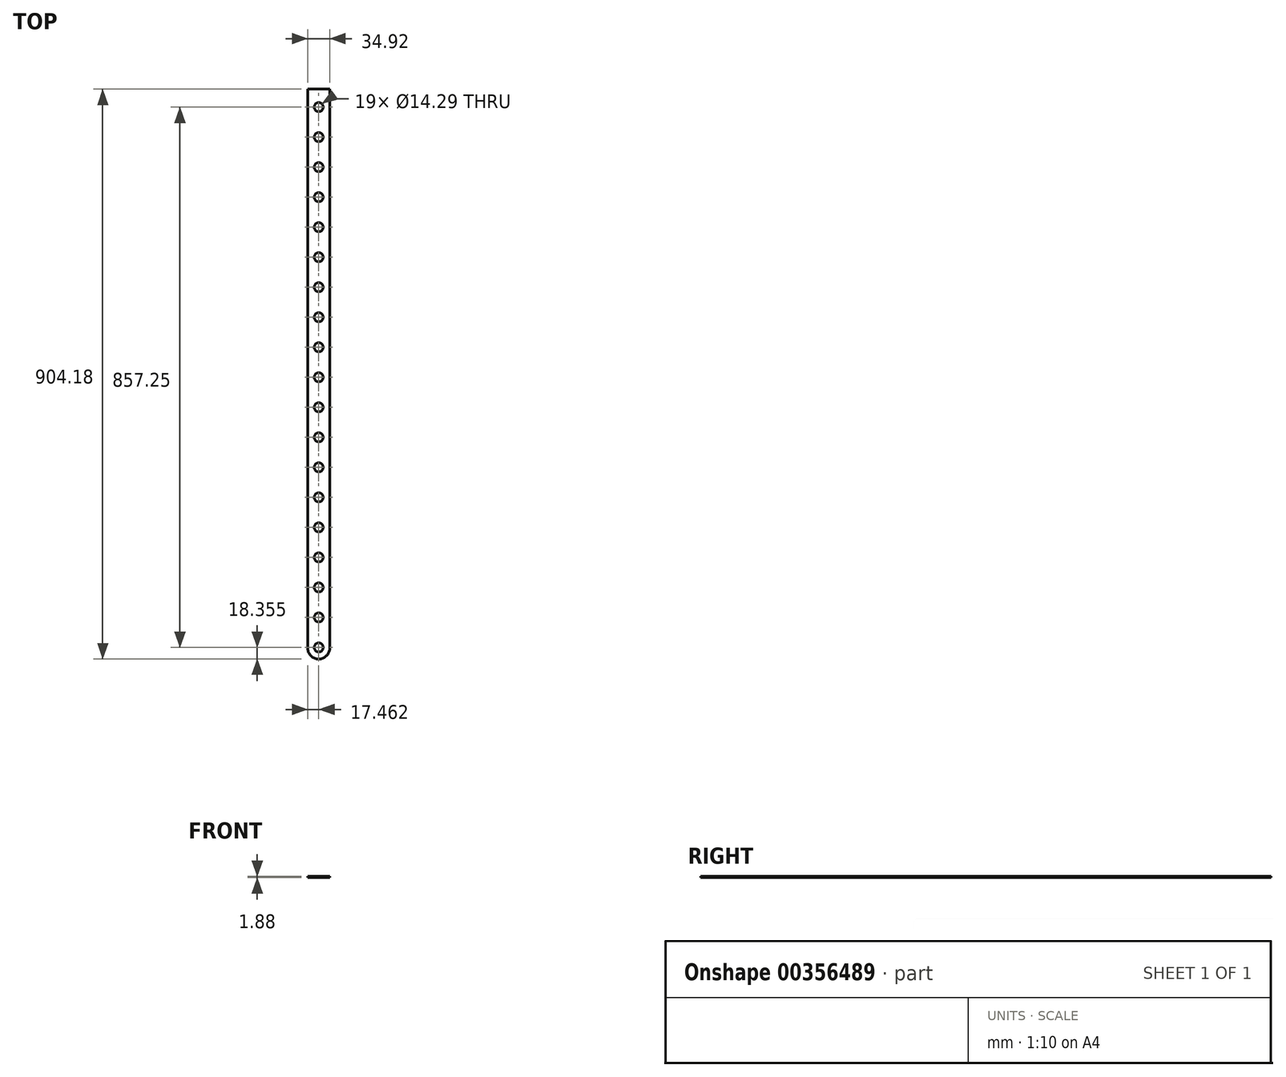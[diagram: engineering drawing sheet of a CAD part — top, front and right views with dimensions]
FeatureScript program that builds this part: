
annotation { "Feature Type Name" : "Feature", "Feature Type Description" : "" }
export const myFeature = defineFeature(function(context is Context, id is Id, definition is map)
    precondition{}
    {
        {
            var Q0;
            Q0=qCreatedBy(makeId("Top.planeOp"),FACE);
            var sketch = newSketch(context, id + "F0", { "sketchPlane" : qUnion([Q0])});
            skLineSegment(sketch, "E0.bottom", {"start": v(0, 0) * mm, "end": v(34.92, 0) * mm});
            skLineSegment(sketch, "E0.top", {"start": v(0, 914.4) * mm, "end": v(34.92, 914.4) * mm});
            skLineSegment(sketch, "E0.left", {"start": v(0, 0) * mm, "end": v(0, 914.4) * mm});
            skLineSegment(sketch, "E0.right", {"start": v(34.93, 0) * mm, "end": v(34.92, 914.4) * mm});
            skCircle(sketch, "E1", {"center": v(17.46, 28.58) * mm, "radius": 7.14 * mm});
            skCircle(sketch, "E2.0.1.0", {"center": v(17.46, 76.2) * mm, "radius": 7.14 * mm});
            skCircle(sketch, "E2.0.2.0", {"center": v(17.46, 123.83) * mm, "radius": 7.14 * mm});
            skCircle(sketch, "E2.0.3.0", {"center": v(17.46, 171.45) * mm, "radius": 7.14 * mm});
            skCircle(sketch, "E2.0.4.0", {"center": v(17.46, 219.08) * mm, "radius": 7.14 * mm});
            skCircle(sketch, "E2.0.5.0", {"center": v(17.46, 266.7) * mm, "radius": 7.14 * mm});
            skCircle(sketch, "E2.0.6.0", {"center": v(17.46, 314.33) * mm, "radius": 7.14 * mm});
            skCircle(sketch, "E2.0.7.0", {"center": v(17.46, 361.95) * mm, "radius": 7.14 * mm});
            skCircle(sketch, "E2.0.8.0", {"center": v(17.46, 409.58) * mm, "radius": 7.14 * mm});
            skCircle(sketch, "E2.0.9.0", {"center": v(17.46, 457.2) * mm, "radius": 7.14 * mm});
            skCircle(sketch, "E2.0.10.0", {"center": v(17.46, 504.83) * mm, "radius": 7.14 * mm});
            skCircle(sketch, "E2.0.11.0", {"center": v(17.46, 552.45) * mm, "radius": 7.14 * mm});
            skCircle(sketch, "E2.0.12.0", {"center": v(17.46, 600.08) * mm, "radius": 7.14 * mm});
            skCircle(sketch, "E2.0.13.0", {"center": v(17.46, 647.7) * mm, "radius": 7.14 * mm});
            skCircle(sketch, "E2.0.14.0", {"center": v(17.46, 695.33) * mm, "radius": 7.14 * mm});
            skCircle(sketch, "E2.0.15.0", {"center": v(17.46, 742.95) * mm, "radius": 7.14 * mm});
            skCircle(sketch, "E2.0.16.0", {"center": v(17.46, 790.58) * mm, "radius": 7.14 * mm});
            skCircle(sketch, "E2.0.17.0", {"center": v(17.46, 838.2) * mm, "radius": 7.14 * mm});
            skCircle(sketch, "E2.0.18.0", {"center": v(17.46, 885.83) * mm, "radius": 7.14 * mm});
            skLineSegment(sketch, "E2.direction1", {"start": v(17.46, 28.58) * mm, "end": v(42.86, 28.58) * mm, "construction": true});
            skLineSegment(sketch, "E2.direction2", {"start": v(17.46, 28.58) * mm, "end": v(17.46, 76.2) * mm, "construction": true});
            skArc(sketch, "E3", {"start": v(0, 28.58) * mm, "mid": v(17.46, 10.22) * mm, "end": v(34.93, 28.58) * mm});
            skPoint(sketch, "E3.startSnap0", {"position": v(30.16, 28.58) * mm});
            skSolve(sketch);
        }
        {
            var Q0;
            Q0=makeQuery(id+"F0.imprint","IMPRINT",FACE,{"disambiguationData":[TD([[makeQuery(id+"F0.imprint","IMPRINT",EDGE,{"derivedFrom":sQuery(id+"F0.wireOp",EDGE,"E0.top")}),-1.0]])]});
            extrude(context, id + "F1", {"entities" : qUnion([Q0]), "depth" : 1.88 * mm});
        }
    });
